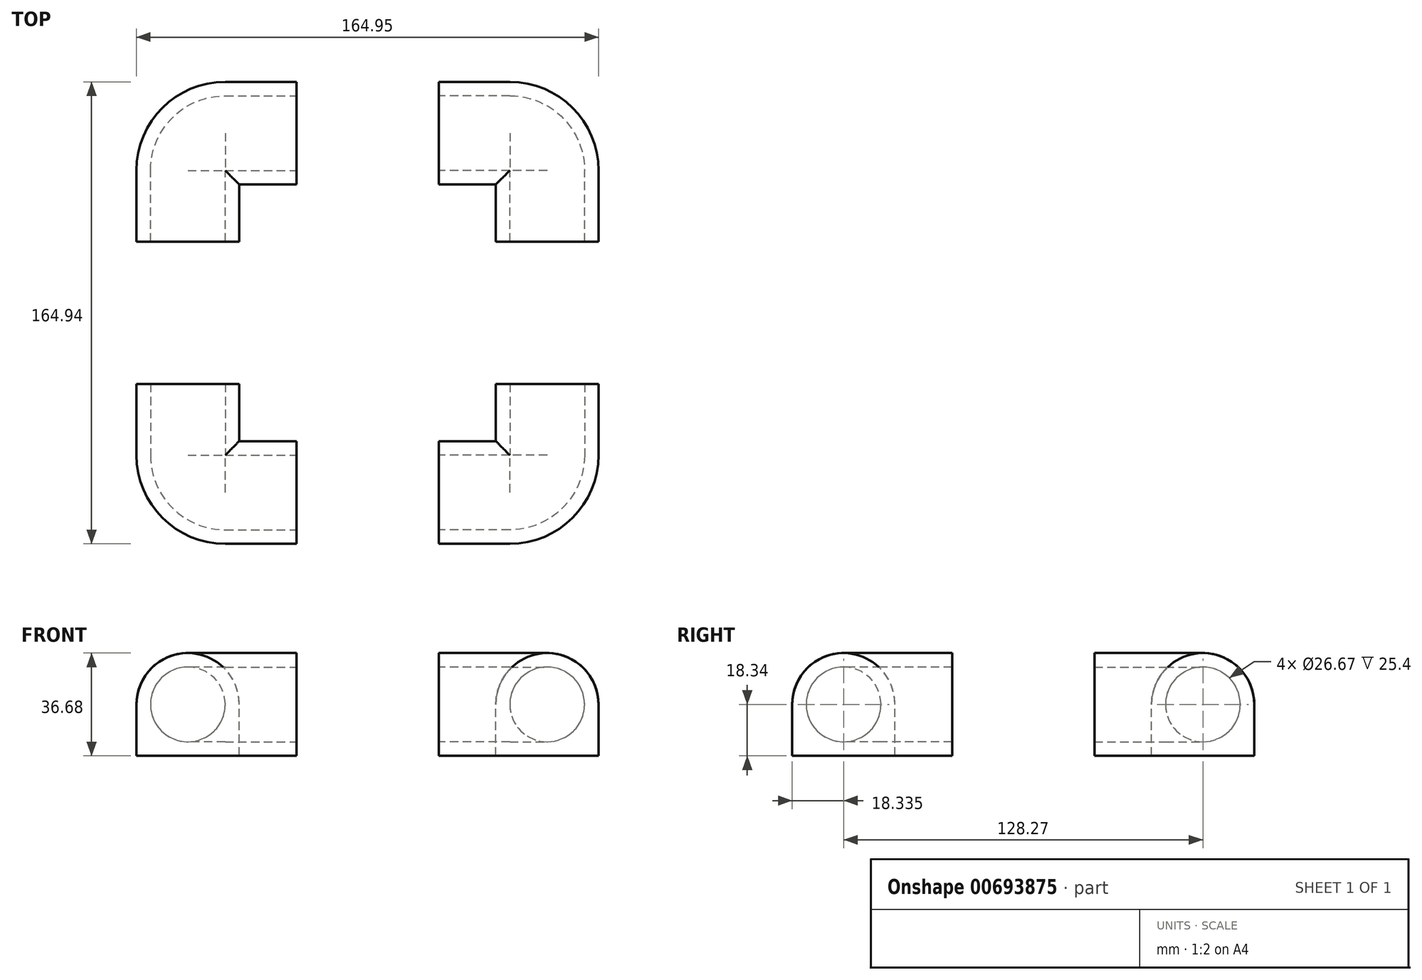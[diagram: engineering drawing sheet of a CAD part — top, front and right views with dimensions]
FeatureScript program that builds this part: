
annotation { "Feature Type Name" : "Feature", "Feature Type Description" : "" }
export const myFeature = defineFeature(function(context is Context, id is Id, definition is map)
    precondition{}
    {
        {
            var Q0;
            Q0=qCreatedBy(makeId("Front.planeOp"),FACE);
            var sketch = newSketch(context, id + "F0", { "sketchPlane" : qUnion([Q0])});
            skCircle(sketch, "E0", {"center": v(0, 0) * mm, "radius": 13.34 * mm});
            skSolve(sketch);
        }
        {
            var Q0;
            Q0=qCreatedBy(makeId("Top.planeOp"),FACE);
            var sketch = newSketch(context, id + "F1", { "sketchPlane" : qUnion([Q0])});
            skLineSegment(sketch, "E1", {"start": v(0, 0) * mm, "end": v(0, -25.4) * mm});
            skLineSegment(sketch, "E2", {"start": v(13.34, -38.73) * mm, "end": v(38.74, -38.73) * mm});
            skArc(sketch, "E3", {"start": v(0, -25.4) * mm, "mid": v(3.9, -34.83) * mm, "end": v(13.34, -38.73) * mm});
            skSolve(sketch);
        }
        {
            var Q0;
            Q0=makeQuery(id+"F0.imprint","IMPRINT",FACE,{"disambiguationData":[TD([[makeQuery(id+"F0.imprint","IMPRINT",EDGE,{"derivedFrom":sQuery(id+"F0.wireOp",EDGE,"E0")}),1.0]])]});
            var Q1;
            Q1=sQuery(id+"F1.wireOp",EDGE,"E1");
            var Q2;
            Q2=sQuery(id+"F1.wireOp",EDGE,"E3");
            var Q3;
            Q3=sQuery(id+"F1.wireOp",EDGE,"E2");
            sweep(context, id + "F2", {"profiles" : qUnion([Q0]), "path" : qUnion([Q1, Q2, Q3])});
        }
        {
            var Q0;
            Q0=makeQuery(id+"F2.opSweep","CAP_FACE",FACE,{"disambiguationData":[OSD([sQuery(id+"F0.wireOp",EDGE,"E0"),sQuery(id+"F1.wireOp",VERTEX,"E2.end")])],"isStart":false});
            var Q1;
            Q1=makeQuery(id+"F2.opSweep","CAP_FACE",FACE,{"disambiguationData":[OSD([sQuery(id+"F0.wireOp",EDGE,"E0"),sQuery(id+"F1.wireOp",VERTEX,"E1.start")])],"isStart":true});
            shell(context, id + "F3", {"entities" : qUnion([Q0, Q1]), "thickness" : 5 * mm, "oppositeDirection" : true});
        }
        {
            var Q0;
            Q0=qCreatedBy(makeId("Top.planeOp"),FACE);
            cPlane(context, id + "F4", {"entities" : qUnion([Q0]), "cplaneType" : CPlaneType.OFFSET, "offset" : 13.33 * mm, "oppositeDirection" : true, "width" : 152.4 * mm, "height" : 152.4 * mm});
        }
        {
            var Q0;
            Q0=qCreatedBy(id+"F4.planeOp",FACE);
            var sketch = newSketch(context, id + "F5", { "sketchPlane" : qUnion([Q0])});
            skLineSegment(sketch, "E4", {"start": v(38.74, -57.07) * mm, "end": v(13.34, -57.07) * mm});
            skLineSegment(sketch, "E5.0", {"start": v(38.74, -20.4) * mm, "end": v(38.74, -57.07) * mm});
            skLineSegment(sketch, "E6", {"start": v(18.33, -20.4) * mm, "end": v(38.74, -20.4) * mm});
            skLineSegment(sketch, "E7", {"start": v(18.34, 0) * mm, "end": v(18.34, -20.4) * mm});
            skArc(sketch, "E8", {"start": v(-18.33, -25.4) * mm, "mid": v(-9.06, -47.8) * mm, "end": v(13.34, -57.07) * mm});
            skLineSegment(sketch, "E9", {"start": v(-18.34, -25.4) * mm, "end": v(-18.34, 0) * mm});
            skLineSegment(sketch, "E10.0", {"start": v(18.34, 0) * mm, "end": v(-18.34, 0) * mm});
            skSolve(sketch);
        }
        {
            var Q0;
            Q0 = qSketchRegion(id + "F5", true);
            var Q1;
            Q1=makeQuery(id+"F2.opSweep","SWEPT_FACE",FACE,{"disambiguationData":[OSD([sQuery(id+"F0.wireOp",EDGE,"E0"),sQuery(id+"F1.wireOp",EDGE,"E1")])]});
            var Q2;
            Q2=makeQuery(id+"F2.opSweep","SWEPT_BODY",BODY,{"disambiguationData":[OSD([sQuery(id+"F0.wireOp",EDGE,"E0"),sQuery(id+"F1.wireOp",EDGE,"E2")])]});
            extrude(context, id + "F6", {"entities" : qUnion([Q0]), "operationType" : NewBodyOperationType.ADD, "oppositeDirection" : true, "depth" : 5 * mm, "offsetDistance" : 25.4 * mm, "hasSecondDirection" : true, "secondDirectionBound" : SecondDirectionBoundingType.UP_TO_BODY, "secondDirectionOppositeDirection" : false, "secondDirectionDepth" : 25.4 * mm, "secondDirectionBoundEntityFace" : qUnion([Q1]), "secondDirectionBoundEntityBody" : qUnion([Q2])});
        }
        {
            var Q0;
            Q0 = qSketchRegion(id + "F0", true);
            var Q1;
            Q1 = qConstructionFilter(qBodyType(qCreatedBy(id + "F1" ,EDGE), BodyType.WIRE), ConstructionObject.NO);
            sweep(context, id + "F7", {"operationType" : NewBodyOperationType.REMOVE, "profiles" : qUnion([Q0]), "path" : qUnion([Q1])});
        }
        {
            var Q0;
            Q0=makeQuery(id+"F2.opSweep","SWEPT_BODY",BODY,{"disambiguationData":[OSD([sQuery(id+"F0.wireOp",EDGE,"E0"),sQuery(id+"F1.wireOp",EDGE,"E2")])]});
            var Q1;
            Q1=qCreatedBy(makeId("Front.planeOp"),FACE);
            mirror(context, id + "F8", {"entities" : qUnion([Q0]), "mirrorPlane" : qUnion([Q1])});
        }
        {
            var Q0;
            Q0=makeQuery(id+"F2.opSweep","SWEPT_BODY",BODY,{"disambiguationData":[OSD([sQuery(id+"F0.wireOp",EDGE,"E0"),sQuery(id+"F1.wireOp",EDGE,"E2")])]});
            var Q1;
            Q1=makeQuery(id+"F8.opPattern","COPY",BODY,{"derivedFrom":makeQuery(id+"F2.opSweep","SWEPT_BODY",BODY,{"disambiguationData":[OSD([sQuery(id+"F0.wireOp",EDGE,"E0"),sQuery(id+"F1.wireOp",EDGE,"E2")])]}),"instanceName":"1"});
            var Q2;
            Q2=makeQuery(id+"F2.opSweep","CAP_FACE",FACE,{"disambiguationData":[OSD([sQuery(id+"F0.wireOp",EDGE,"E0"),sQuery(id+"F1.wireOp",VERTEX,"E2.end")])],"isStart":false});
            mirror(context, id + "F9", {"entities" : qUnion([Q0, Q1]), "mirrorPlane" : qUnion([Q2])});
        }
        {
            var Q0;
            Q0=makeQuery(id+"F9.opPattern","COPY",BODY,{"derivedFrom":makeQuery(id+"F8.opPattern","COPY",BODY,{"derivedFrom":makeQuery(id+"F2.opSweep","SWEPT_BODY",BODY,{"disambiguationData":[OSD([sQuery(id+"F0.wireOp",EDGE,"E0"),sQuery(id+"F1.wireOp",EDGE,"E2")])]}),"instanceName":"1"}),"instanceName":"1"});
            var Q1;
            Q1=makeQuery(id+"F8.opPattern","COPY",BODY,{"derivedFrom":makeQuery(id+"F2.opSweep","SWEPT_BODY",BODY,{"disambiguationData":[OSD([sQuery(id+"F0.wireOp",EDGE,"E0"),sQuery(id+"F1.wireOp",EDGE,"E2")])]}),"instanceName":"1"});
            transform(context, id + "F10", {"entities" : qUnion([Q0, Q1]), "transformType" : TransformType.TRANSLATION_3D, "dx" : 0 * mm, "dy" : 50.8 * mm, "dz" : 0 * mm, "makeCopy" : false});
        }
        {
            var Q0;
            Q0=makeQuery(id+"F9.opPattern","COPY",BODY,{"derivedFrom":makeQuery(id+"F2.opSweep","SWEPT_BODY",BODY,{"disambiguationData":[OSD([sQuery(id+"F0.wireOp",EDGE,"E0"),sQuery(id+"F1.wireOp",EDGE,"E2")])]}),"instanceName":"1"});
            var Q1;
            Q1=makeQuery(id+"F9.opPattern","COPY",BODY,{"derivedFrom":makeQuery(id+"F8.opPattern","COPY",BODY,{"derivedFrom":makeQuery(id+"F2.opSweep","SWEPT_BODY",BODY,{"disambiguationData":[OSD([sQuery(id+"F0.wireOp",EDGE,"E0"),sQuery(id+"F1.wireOp",EDGE,"E2")])]}),"instanceName":"1"}),"instanceName":"1"});
            transform(context, id + "F11", {"entities" : qUnion([Q0, Q1]), "transformType" : TransformType.TRANSLATION_3D, "dx" : 50.8 * mm, "dy" : 0 * mm, "dz" : 0 * mm, "makeCopy" : false});
        }
    });
